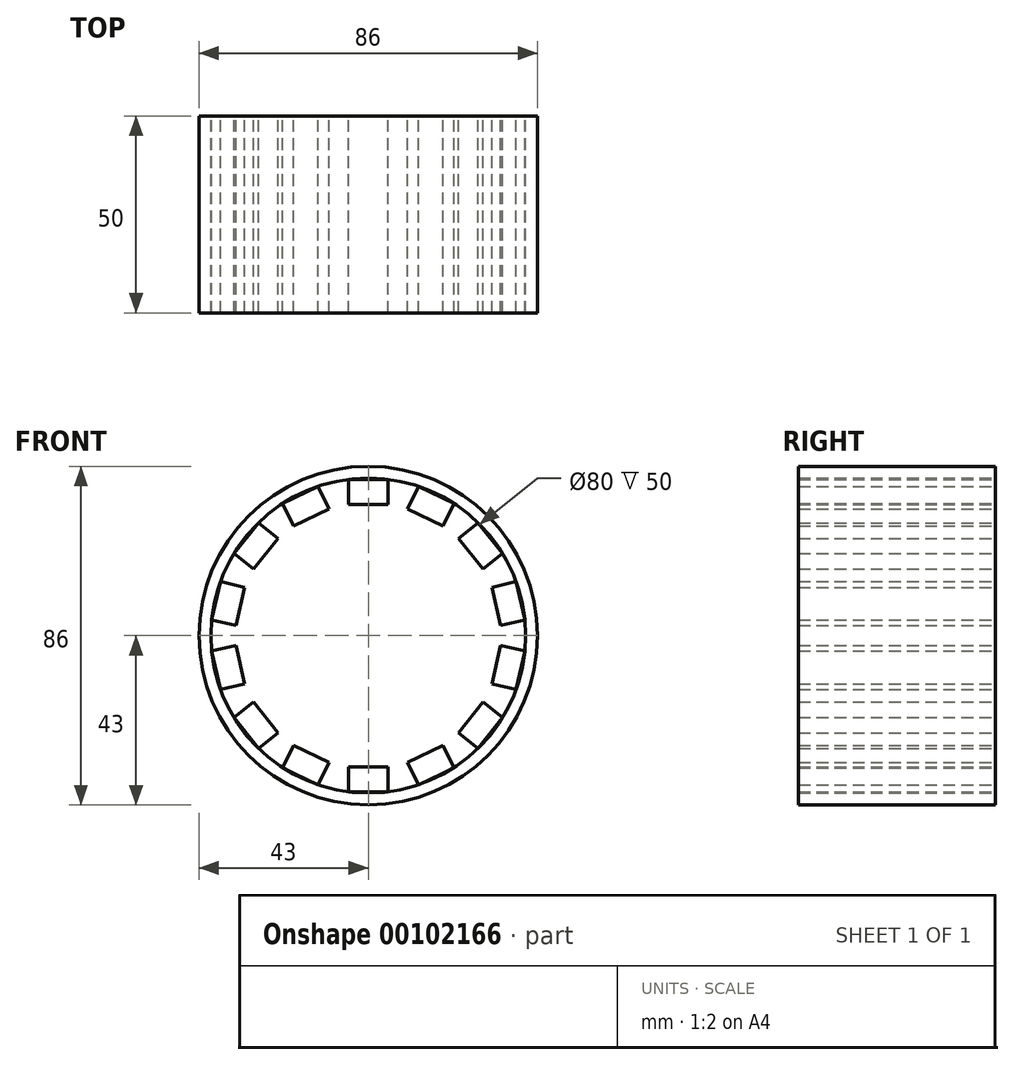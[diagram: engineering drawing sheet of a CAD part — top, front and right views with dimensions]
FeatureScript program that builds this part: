
annotation { "Feature Type Name" : "Feature", "Feature Type Description" : "" }
export const myFeature = defineFeature(function(context is Context, id is Id, definition is map)
    precondition{}
    {
        {
            var Q0;
            Q0=qCreatedBy(makeId("Front.planeOp"),FACE);
            var sketch = newSketch(context, id + "F0", { "sketchPlane" : qUnion([Q0])});
            skLineSegment(sketch, "E0.bottom", {"start": v(-5, 39.69) * mm, "end": v(5, 39.69) * mm});
            skLineSegment(sketch, "E0.top", {"start": v(-5, 33.34) * mm, "end": v(5, 33.34) * mm});
            skLineSegment(sketch, "E0.left", {"start": v(-5, 39.69) * mm, "end": v(-5, 33.34) * mm});
            skLineSegment(sketch, "E0.right", {"start": v(5, 39.69) * mm, "end": v(5, 33.34) * mm});
            skPoint(sketch, "E1", {"position": v(0, 33.34) * mm});
            skCircle(sketch, "E2", {"center": v(0, 0) * mm, "radius": 40 * mm, "construction": true});
            skLineSegment(sketch, "E3", {"start": v(0, 0) * mm, "end": v(5, 39.69) * mm});
            skSolve(sketch);
        }
        {
            var Q0;
            {var subQ0=sQuery(id+"F0.wireOp",EDGE,"E0.bottom");Q0=makeQuery(id+"F0.imprint","IMPRINT",FACE,{"disambiguationData":[TD([[makeQuery(id+"F0.imprint","IMPRINT",EDGE,{"derivedFrom":subQ0}),-1.0]])]});}
            var Q1;
            {var subQ0=sQuery(id+"F0.wireOp",EDGE,"E0.right");Q1=makeQuery(id+"F0.imprint","IMPRINT",FACE,{"disambiguationData":[TD([[makeQuery(id+"F0.imprint","IMPRINT",EDGE,{"derivedFrom":subQ0}),-1.0]])]});}
            extrude(context, id + "F1", {"entities" : qUnion([Q0, Q1]), "endBound" : BoundingType.SYMMETRIC, "depth" : 50 * mm});
        }
        {
            var Q0;
            Q0=qCreatedBy(makeId("Top.planeOp"),FACE);
            var sketch = newSketch(context, id + "F2", { "sketchPlane" : qUnion([Q0])});
            skLineSegment(sketch, "E4", {"start": v(0, 0) * mm, "end": v(0, -113.24) * mm});
            skSolve(sketch);
        }
        {
            var Q0;
            Q0=makeQuery(id+"F1.opExtrude","SWEPT_BODY",BODY,{"disambiguationData":[OSD([sQuery(id+"F0.wireOp",EDGE,"E0.bottom"),sQuery(id+"F0.wireOp",EDGE,"E0.top"),sQuery(id+"F0.wireOp",EDGE,"E0.left"),sQuery(id+"F0.wireOp",EDGE,"E3")])]});
            var Q1;
            Q1=sQuery(id+"F2.wireOp",EDGE,"E4");
            circularPattern(context, id + "F3", {"entities" : qUnion([Q0]), "axis" : qUnion([Q1]), "angle" : 360 * degree, "instanceCount" : 14, "equalSpace" : true});
        }
        {
            var Q0;
            Q0=qCreatedBy(makeId("Front.planeOp"),FACE);
            var sketch = newSketch(context, id + "F4", { "sketchPlane" : qUnion([Q0])});
            skPoint(sketch, "E5.0", {"position": v(-27.91, -28.65) * mm});
            skCircle(sketch, "E5.1", {"center": v(0, 0) * mm, "radius": 40 * mm});
            skCircle(sketch, "E6.0", {"center": v(0, 0) * mm, "radius": 43 * mm});
            skSolve(sketch);
        }
        {
            var Q0;
            Q0=makeQuery(id+"F4.imprint","IMPRINT",FACE,{"disambiguationData":[TD([[makeQuery(id+"F4.imprint","IMPRINT",EDGE,{"derivedFrom":sQuery(id+"F4.wireOp",EDGE,"E5.1")}),-1.0]])]});
            extrude(context, id + "F5", {"entities" : qUnion([Q0]), "endBound" : BoundingType.SYMMETRIC, "depth" : 50 * mm});
        }
    });
